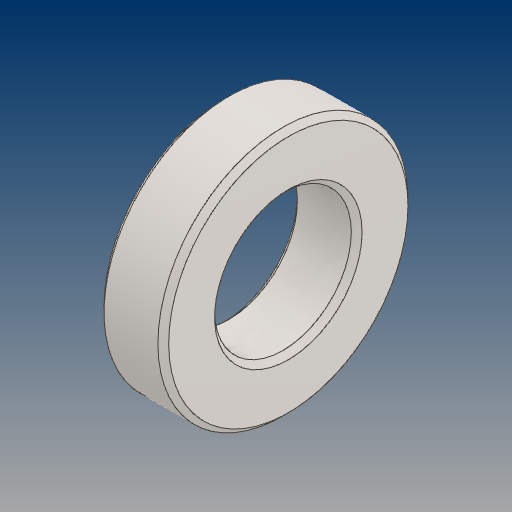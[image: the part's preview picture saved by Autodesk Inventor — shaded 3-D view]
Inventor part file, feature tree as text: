
AUTODESK INVENTOR PART (.ipt)
format: ipt  version: 2021 (Build 250183000, 183)  size: 125,952 bytes
history: native  units: mm
features: chamfer x1
ambient origin geometry x8: Origin, YZ Plane, XZ Plane, XY Plane, X Axis, Y Axis, Z Axis, Center Point
bodies: Solid1 (feature_tree)
feature tree (1):
  chamfer  "Chamfer1"  [1 undecoded]
note: 1 required parameter value undecoded (feature->parameter linkage not recoverable at this tier; creation-order binding heuristic only, values carry confidence <= 0.55)
